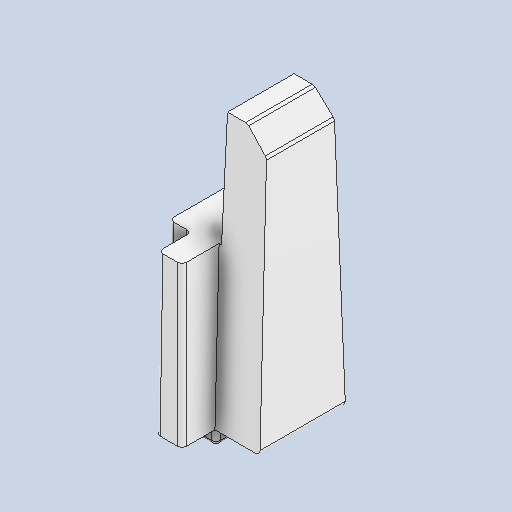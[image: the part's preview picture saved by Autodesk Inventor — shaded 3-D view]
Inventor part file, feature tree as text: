
AUTODESK INVENTOR PART (.ipt)
format: ipt  version: 2024.2 (Build 282272000, 272)  size: 171,008 bytes
history: native  units: in
note: dims shown in document units (in); Inventor stores cm internally (conversion verified against a paired STEP export)
features: fillet x1
ambient origin geometry x8: Origin, YZ Plane, XZ Plane, XY Plane, X Axis, Y Axis, Z Axis, Center Point
bodies: Solid1 (feature_tree)
feature tree (1):
  fillet  "Fillet4"  [1 undecoded]
note: 1 required parameter value undecoded (feature->parameter linkage not recoverable at this tier; creation-order binding heuristic only, values carry confidence <= 0.55)
